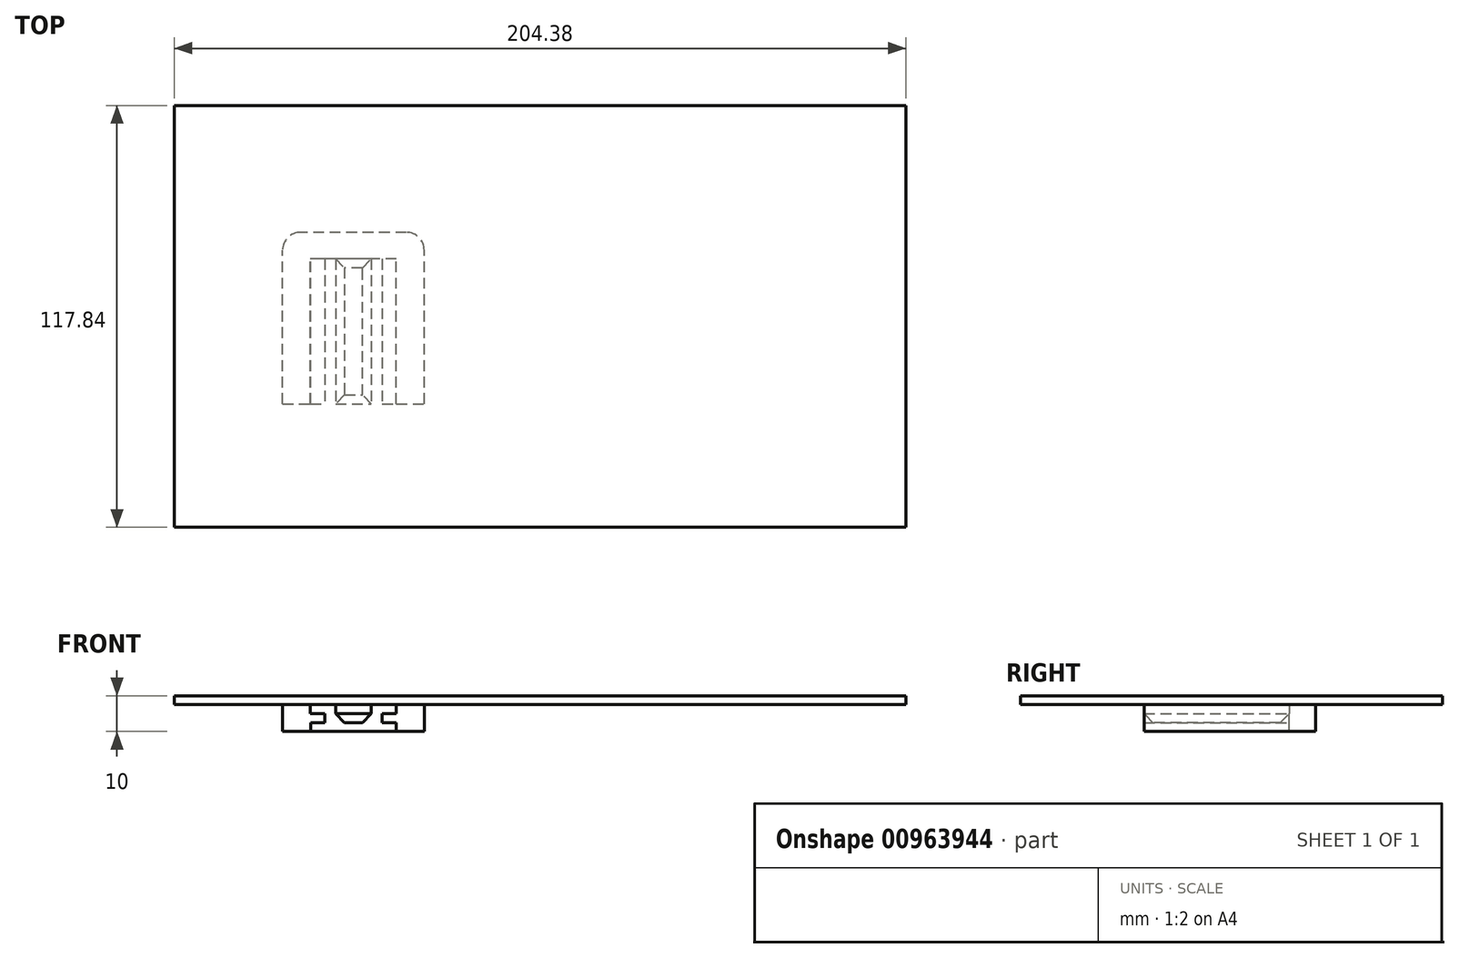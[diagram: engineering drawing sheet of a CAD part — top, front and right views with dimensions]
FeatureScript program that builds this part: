
annotation { "Feature Type Name" : "Feature", "Feature Type Description" : "" }
export const myFeature = defineFeature(function(context is Context, id is Id, definition is map)
    precondition{}
    {
        {
            var Q0;
            Q0=qCreatedBy(makeId("Top.planeOp"),FACE);
            var sketch = newSketch(context, id + "F0", { "sketchPlane" : qUnion([Q0])});
            skLineSegment(sketch, "E0.bottom", {"start": v(11.5, -20) * mm, "end": v(-11.5, -20) * mm});
            skLineSegment(sketch, "E0.top", {"start": v(11.5, 20) * mm, "end": v(-11.5, 20) * mm});
            skLineSegment(sketch, "E0.left", {"start": v(11.5, -20) * mm, "end": v(11.5, 20) * mm});
            skLineSegment(sketch, "E0.right", {"start": v(-11.5, -20) * mm, "end": v(-11.5, 12.5) * mm});
            skPoint(sketch, "E0.middle", {"position": v(0, 0) * mm});
            skLineSegment(sketch, "E1", {"start": v(5.5, 20) * mm, "end": v(5.5, 16.5) * mm});
            skLineSegment(sketch, "E2", {"start": v(-5.5, 20) * mm, "end": v(-5.5, -20) * mm});
            skLineSegment(sketch, "E3", {"start": v(-11.5, 16.5) * mm, "end": v(-7.5, 16.5) * mm});
            skLineSegment(sketch, "E4", {"start": v(-7.5, 16.5) * mm, "end": v(-11.5, 12.5) * mm});
            skLineSegment(sketch, "E5", {"start": v(5.5, 16.5) * mm, "end": v(9.5, 16.5) * mm});
            skLineSegment(sketch, "E6", {"start": v(9.5, 16.5) * mm, "end": v(5.5, 12.5) * mm});
            skLineSegment(sketch, "E7.trimOffspring", {"start": v(-11.5, 16.5) * mm, "end": v(-11.5, 20) * mm});
            skLineSegment(sketch, "E8.trimOffspring", {"start": v(5.5, 12.5) * mm, "end": v(5.5, -20) * mm});
            skSolve(sketch);
        }
        {
            var Q0;
            Q0=qCreatedBy(makeId("Top.planeOp"),FACE);
            var sketch = newSketch(context, id + "F1", { "sketchPlane" : qUnion([Q0])});
            skLineSegment(sketch, "E9.0", {"start": v(-12, 16) * mm, "end": v(-12, 20.5) * mm});
            skLineSegment(sketch, "E9.1", {"start": v(-12, -20.5) * mm, "end": v(-12, 12.7) * mm});
            skLineSegment(sketch, "E9.3", {"start": v(12, -20.5) * mm, "end": v(12, 20.5) * mm});
            skLineSegment(sketch, "E9.4", {"start": v(12, 20.5) * mm, "end": v(5, 20.5) * mm});
            skLineSegment(sketch, "E10.0", {"start": v(-12, 16) * mm, "end": v(-8.7, 16) * mm});
            skLineSegment(sketch, "E11.0", {"start": v(-8.7, 16) * mm, "end": v(-12, 12.7) * mm});
            skLineSegment(sketch, "E12.0", {"start": v(-5, 20.5) * mm, "end": v(-5, -20.5) * mm});
            skLineSegment(sketch, "E13.0", {"start": v(5, 12.7) * mm, "end": v(5, -20.5) * mm});
            skLineSegment(sketch, "E14.0", {"start": v(5, 20.5) * mm, "end": v(5, 16) * mm});
            skLineSegment(sketch, "E15.0", {"start": v(5, 16) * mm, "end": v(8.3, 16) * mm});
            skLineSegment(sketch, "E16.0", {"start": v(8.3, 16) * mm, "end": v(5, 12.7) * mm});
            skLineSegment(sketch, "E17.bottom", {"start": v(19.77, -27.93) * mm, "end": v(-19.77, -27.93) * mm});
            skLineSegment(sketch, "E17.top", {"start": v(19.77, 27.93) * mm, "end": v(-19.77, 27.93) * mm});
            skLineSegment(sketch, "E17.left", {"start": v(19.77, -27.93) * mm, "end": v(19.77, 27.93) * mm});
            skLineSegment(sketch, "E17.right", {"start": v(-19.77, -27.93) * mm, "end": v(-19.77, 27.93) * mm});
            skPoint(sketch, "E17.middle", {"position": v(0, 0) * mm});
            skLineSegment(sketch, "E18", {"start": v(-12, -20.5) * mm, "end": v(-12, -27.93) * mm});
            skLineSegment(sketch, "E19", {"start": v(-5, -20.5) * mm, "end": v(-5, -27.93) * mm});
            skLineSegment(sketch, "E20", {"start": v(5, -20.5) * mm, "end": v(5, -27.93) * mm});
            skLineSegment(sketch, "E21", {"start": v(12, -20.5) * mm, "end": v(12, -27.93) * mm});
            skLineSegment(sketch, "E22.trimOffspring", {"start": v(-5, 20.5) * mm, "end": v(-12, 20.5) * mm});
            skLineSegment(sketch, "E23", {"start": v(-19.77, -20) * mm, "end": v(19.77, -20) * mm});
            skLineSegment(sketch, "E24", {"start": v(-8, 20.5) * mm, "end": v(-8, -20) * mm});
            skLineSegment(sketch, "E25", {"start": v(8, 20.5) * mm, "end": v(8, -20) * mm});
            skLineSegment(sketch, "E26", {"start": v(5, 12.7) * mm, "end": v(5, 16) * mm});
            skLineSegment(sketch, "E27", {"start": v(-5, 20.5) * mm, "end": v(5, 20.5) * mm});
            skLineSegment(sketch, "E28", {"start": v(-12, 16) * mm, "end": v(-12, 12.7) * mm});
            skSolve(sketch);
        }
        {
            var Q0;
            Q0=makeQuery(id+"F1.imprint","IMPRINT",FACE,{"disambiguationData":[TD([[makeQuery(id+"F1.imprint","IMPRINT",EDGE,{"derivedFrom":sQuery(id+"F1.wireOp",EDGE,"E9.0")}),1.0]])]});
            var Q1;
            Q1=makeQuery(id+"F1.imprint","IMPRINT",FACE,{"disambiguationData":[TD([[makeQuery(id+"F1.imprint","IMPRINT",EDGE,{"derivedFrom":sQuery(id+"F1.wireOp",EDGE,"E14.0")}),-1.0]])]});
            extrude(context, id + "F2", {"entities" : qUnion([Q0, Q1]), "depth" : 2.5 * mm, "offsetDistance" : 25 * mm});
        }
        {
            var Q0;
            {var subQ5=sQuery(id+"F1.wireOp",EDGE,"E9.4");var subQ6=sQuery(id+"F1.wireOp",EDGE,"E9.3");var subQ7=makeQuery(id+"F1.imprint","INTERSECT",VERTEX,{"derivedFrom":[subQ6,subQ5]});Q0=makeQuery(id+"F1.imprint","IMPRINT",FACE,{"disambiguationData":[TD([[makeQuery(id+"F1.imprint","IMPRINT",EDGE,{"disambiguationData":[TD([[subQ7,1.0]])],"derivedFrom":subQ6}),1.0]])]});}
            var Q1;
            {var subQ17=sQuery(id+"F1.wireOp",EDGE,"E9.0");Q1=makeQuery(id+"F1.imprint","IMPRINT",FACE,{"disambiguationData":[TD([[makeQuery(id+"F1.imprint","IMPRINT",EDGE,{"derivedFrom":subQ17}),1.0]])]});}
            var Q2;
            {var subQ0=sQuery(id+"F1.wireOp",EDGE,"E16.0");var subQ1=sQuery(id+"F1.wireOp",EDGE,"E15.0");var subQ2=makeQuery(id+"F1.imprint","INTERSECT",VERTEX,{"derivedFrom":[subQ1,subQ0]});Q2=makeQuery(id+"F1.imprint","IMPRINT",FACE,{"disambiguationData":[TD([[makeQuery(id+"F1.imprint","IMPRINT",EDGE,{"disambiguationData":[TD([[subQ2,1.0]])],"derivedFrom":subQ1}),-1.0]])]});}
            var Q3;
            {var subQ5=sQuery(id+"F1.wireOp",EDGE,"E9.0");Q3=makeQuery(id+"F1.imprint","IMPRINT",FACE,{"disambiguationData":[TD([[makeQuery(id+"F1.imprint","IMPRINT",EDGE,{"derivedFrom":subQ5}),-1.0]])]});}
            var Q4;
            Q4=makeQuery(id+"F1.imprint","IMPRINT",FACE,{"disambiguationData":[TD([[makeQuery(id+"F1.imprint","IMPRINT",EDGE,{"derivedFrom":sQuery(id+"F1.wireOp",EDGE,"E10.0")}),-1.0]])]});
            extrude(context, id + "F3", {"entities" : qUnion([Q0, Q1, Q2, Q3, Q4]), "operationType" : NewBodyOperationType.ADD, "oppositeDirection" : true, "depth" : 2.5 * mm, "offsetDistance" : 25 * mm});
        }
        {
            var Q0;
            Q0=makeQuery(id+"F1.imprint","IMPRINT",FACE,{"disambiguationData":[TD([[makeQuery(id+"F1.imprint","IMPRINT",EDGE,{"derivedFrom":sQuery(id+"F1.wireOp",EDGE,"E14.0")}),-1.0]])]});
            extrude(context, id + "F4", {"entities" : qUnion([Q0]), "operationType" : NewBodyOperationType.ADD, "oppositeDirection" : true, "depth" : 2.5 * mm, "offsetDistance" : 25 * mm, "hasDraft" : true, "draftAngle" : 45 * degree, "draftPullDirection" : true});
        }
        {
            var Q0;
            Q0=makeQuery(id+"F3.opExtrude","CAP_FACE",FACE,{"disambiguationData":[OSD([sQuery(id+"F1.wireOp",EDGE,"E9.4"),sQuery(id+"F1.wireOp",EDGE,"E17.top"),sQuery(id+"F1.wireOp",EDGE,"E17.left"),sQuery(id+"F1.wireOp",EDGE,"E17.right"),sQuery(id+"F1.wireOp",EDGE,"E22.trimOffspring"),sQuery(id+"F1.wireOp",EDGE,"E23"),sQuery(id+"F1.wireOp",EDGE,"E24"),sQuery(id+"F1.wireOp",EDGE,"E25"),sQuery(id+"F1.wireOp",EDGE,"E27")])],"isStart":false});
            var sketch = newSketch(context, id + "F5", { "sketchPlane" : qUnion([Q0])});
            skLineSegment(sketch, "E29", {"start": v(-11.97, 20) * mm, "end": v(-11.97, -27.93) * mm});
            skLineSegment(sketch, "E30", {"start": v(12, 20) * mm, "end": v(12, -27.93) * mm});
            skLineSegment(sketch, "E31", {"start": v(8, -20.5) * mm, "end": v(19.77, -20.5) * mm});
            skLineSegment(sketch, "E32", {"start": v(19.77, -20.5) * mm, "end": v(-19.77, -20.5) * mm});
            skSolve(sketch);
        }
        {
            var Q0;
            {var subQ0=sQuery(id+"F5.wireOp",EDGE,"E29");Q0=makeQuery(id+"F5.imprint","IMPRINT",FACE,{"disambiguationData":[TD([[makeQuery(id+"F5.imprint","IMPRINT",EDGE,{"derivedFrom":subQ0}),-1.0]])]});}
            var Q1;
            {var subQ0=sQuery(id+"F5.wireOp",EDGE,"E30");Q1=makeQuery(id+"F5.imprint","IMPRINT",FACE,{"disambiguationData":[TD([[makeQuery(id+"F5.imprint","IMPRINT",EDGE,{"derivedFrom":subQ0}),1.0]])]});}
            var Q2;
            {var subQ4=makeQuery(id+"F3.opExtrude","CAP_EDGE",EDGE,{"disambiguationData":[OSD([sQuery(id+"F1.wireOp",EDGE,"E17.top")])],"isStart":false});var subQ7=sQuery(id+"F5.wireOp",EDGE,"E29");var subQ8=makeQuery(id+"F5.imprint","INTERSECT",VERTEX,{"derivedFrom":[subQ4,subQ7]});Q2=makeQuery(id+"F5.imprint","IMPRINT",FACE,{"disambiguationData":[TD([[makeQuery(id+"F5.imprint","IMPRINT",EDGE,{"disambiguationData":[TD([[subQ8,1.0]])],"derivedFrom":subQ7}),1.0]])]});}
            extrude(context, id + "F6", {"entities" : qUnion([Q0, Q1, Q2]), "operationType" : NewBodyOperationType.ADD, "depth" : 2.5 * mm, "offsetDistance" : 25 * mm});
        }
        {
            var Q0;
            {var subQ0=sQuery(id+"F1.wireOp",EDGE,"E17.right");var subQ1=sQuery(id+"F1.wireOp",EDGE,"E17.top");Q0=makeQuery(id+"F6.boolean.opBoolean","MERGE",EDGE,{"derivedFrom":[makeQuery(id+"F3.boolean.opBoolean","MERGE",EDGE,{"derivedFrom":[makeQuery(id+"F2.opExtrude","SWEPT_EDGE",EDGE,{"disambiguationData":[OSD([subQ1,subQ0])]}),makeQuery(id+"F3.opExtrude","SWEPT_EDGE",EDGE,{"disambiguationData":[OSD([subQ1,subQ0])]})]}),makeQuery(id+"F6.opExtrude","SWEPT_EDGE",EDGE,{"disambiguationData":[OSD([subQ1,subQ0])]})]});}
            var Q1;
            {var subQ0=sQuery(id+"F1.wireOp",EDGE,"E17.left");var subQ1=sQuery(id+"F1.wireOp",EDGE,"E17.top");Q1=makeQuery(id+"F6.boolean.opBoolean","MERGE",EDGE,{"derivedFrom":[makeQuery(id+"F3.boolean.opBoolean","MERGE",EDGE,{"derivedFrom":[makeQuery(id+"F2.opExtrude","SWEPT_EDGE",EDGE,{"disambiguationData":[OSD([subQ1,subQ0])]}),makeQuery(id+"F3.opExtrude","SWEPT_EDGE",EDGE,{"disambiguationData":[OSD([subQ1,subQ0])]})]}),makeQuery(id+"F6.opExtrude","SWEPT_EDGE",EDGE,{"disambiguationData":[OSD([subQ1,subQ0])]})]});}
            fillet(context, id + "F7", {"entities" : qUnion([Q0, Q1]), "radius" : 5 * mm, "tangentPropagation" : true, "allowEdgeOverflow" : false});
        }
        {
            var Q0;
            Q0=makeQuery(id+"F2.opExtrude","CAP_FACE",FACE,{"disambiguationData":[OSD([sQuery(id+"F1.wireOp",EDGE,"E9.0"),sQuery(id+"F1.wireOp",EDGE,"E9.1"),sQuery(id+"F1.wireOp",EDGE,"E9.3"),sQuery(id+"F1.wireOp",EDGE,"E9.4"),sQuery(id+"F1.wireOp",EDGE,"E12.0"),sQuery(id+"F1.wireOp",EDGE,"E13.0"),sQuery(id+"F1.wireOp",EDGE,"E14.0"),sQuery(id+"F1.wireOp",EDGE,"E17.top"),sQuery(id+"F1.wireOp",EDGE,"E17.left"),sQuery(id+"F1.wireOp",EDGE,"E17.right"),sQuery(id+"F1.wireOp",EDGE,"E22.trimOffspring"),sQuery(id+"F1.wireOp",EDGE,"E23"),sQuery(id+"F1.wireOp",EDGE,"E26"),sQuery(id+"F1.wireOp",EDGE,"E28")])],"isStart":false});
            var sketch = newSketch(context, id + "F8", { "sketchPlane" : qUnion([Q0])});
            skPoint(sketch, "E33.middle", {"position": v(0, 0) * mm});
            skLineSegment(sketch, "E34.bottom", {"start": v(-50.04, 63.36) * mm, "end": v(154.34, 63.36) * mm});
            skLineSegment(sketch, "E34.top", {"start": v(-50.04, -54.48) * mm, "end": v(154.34, -54.48) * mm});
            skLineSegment(sketch, "E34.left", {"start": v(-50.04, 63.36) * mm, "end": v(-50.04, -54.48) * mm});
            skLineSegment(sketch, "E34.right", {"start": v(154.34, 63.36) * mm, "end": v(154.34, -54.48) * mm});
            skSolve(sketch);
        }
        {
            var Q0;
            {var subQ3=sQuery(id+"F1.wireOp",EDGE,"E9.3");Q0=makeQuery(id+"F8.imprint","IMPRINT",FACE,{"disambiguationData":[TD([[makeQuery(id+"F8.imprint","IMPRINT",EDGE,{"derivedFrom":makeQuery(id+"F2.opExtrude","CAP_EDGE",EDGE,{"disambiguationData":[OSD([subQ3])],"isStart":false})}),-1.0]])]});}
            var Q1;
            Q1=makeQuery(id+"F8.imprint","IMPRINT",FACE,{"disambiguationData":[TD([[makeQuery(id+"F8.imprint","IMPRINT",EDGE,{"derivedFrom":sQuery(id+"F8.wireOp",EDGE,"E34.bottom")}),-1.0]])]});
            extrude(context, id + "F9", {"entities" : qUnion([Q0, Q1]), "operationType" : NewBodyOperationType.ADD, "depth" : 2.5 * mm, "offsetDistance" : 25 * mm});
        }
    });
